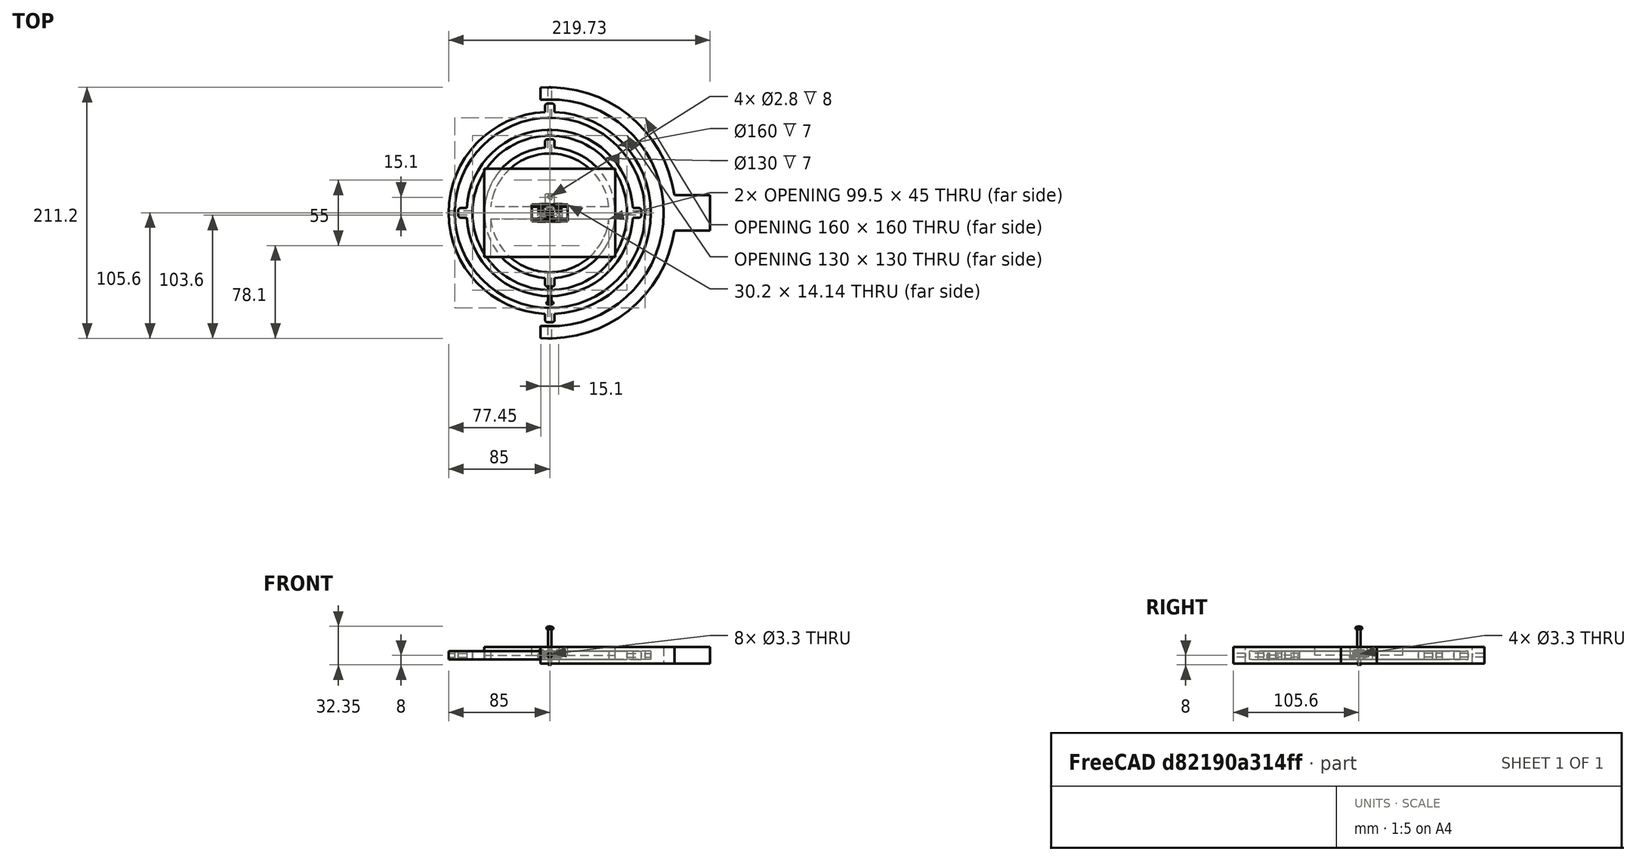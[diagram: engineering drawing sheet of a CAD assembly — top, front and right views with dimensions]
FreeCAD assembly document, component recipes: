
FREECAD ASSEMBLY — COMPONENT RECIPES ("calibration_jig_v1")

This assembly document has 17 components, labeled P0..P16 below (a component is one placed body or linked part). 10 of them carry a construction recipe — the FreeCAD feature program that regenerates the part from scratch, quoted from this document or its linked companion documents; the rest are supplied as boundary geometry only. No exploded tour is included for this assembly.
COMPONENT P0 — geometry summary ("GY_511_LSM303DLHC001"; no construction recipe available for this part):
  bounding box: 21.0 x 16.0 x 3.8 mm
  tessellated surface: 12,790 triangles
  volume: 549 mm^3 (43% of its bounding box)
COMPONENT P1 — geometry summary ("M3-Nut001"; no construction recipe available for this part):
  bounding box: 6.4 x 5.5 x 2.4 mm
  tessellated surface: 2,004 triangles
  volume: 51 mm^3 (60% of its bounding box)
  symmetry: 2-fold rotationally symmetric about the x axis; 2-fold rotationally symmetric about the y axis; 2-fold rotationally symmetric about the z axis; mirror-symmetric across its x mid-plane, y mid-plane, z mid-plane
COMPONENT P2 — geometry summary ("M3-Nut002"; no construction recipe available for this part):
  bounding box: 6.4 x 5.5 x 2.4 mm
  tessellated surface: 2,004 triangles
  volume: 51 mm^3 (60% of its bounding box)
  symmetry: 2-fold rotationally symmetric about the x axis; 2-fold rotationally symmetric about the y axis; 2-fold rotationally symmetric about the z axis; mirror-symmetric across its x mid-plane, y mid-plane, z mid-plane
COMPONENT P3 — geometry summary ("M3-Nut003"; no construction recipe available for this part):
  bounding box: 6.4 x 5.5 x 2.4 mm
  tessellated surface: 2,004 triangles
  volume: 51 mm^3 (60% of its bounding box)
  symmetry: 2-fold rotationally symmetric about the x axis; 2-fold rotationally symmetric about the y axis; 2-fold rotationally symmetric about the z axis; mirror-symmetric across its x mid-plane, y mid-plane, z mid-plane
COMPONENT P4 — geometry summary ("M3x20-Screw003"; no construction recipe available for this part):
  bounding box: 27.3 x 5.6 x 5.6 mm
  tessellated surface: 3,442 triangles
  volume: 221 mm^3 (26% of its bounding box)
  symmetry: 4-fold rotationally symmetric about the x axis; mirror-symmetric across its y mid-plane
COMPONENT P5 — geometry summary ("M3x20-Screw002"; no construction recipe available for this part):
  bounding box: 27.3 x 5.6 x 5.6 mm
  tessellated surface: 3,442 triangles
  volume: 221 mm^3 (26% of its bounding box)
  symmetry: 2-fold rotationally symmetric about the z axis; mirror-symmetric across its y mid-plane
COMPONENT P6 — geometry summary ("M3x25-Screw001"; no construction recipe available for this part):
  bounding box: 32.3 x 5.6 x 5.6 mm
  tessellated surface: 3,622 triangles
  volume: 256 mm^3 (25% of its bounding box)
  symmetry: 4-fold rotationally symmetric about the x axis; mirror-symmetric across its y mid-plane, z mid-plane
COMPONENT P7 — recipe-attached ("base001", modeled in this document).
Construction recipe (the document's own serialized feature program — sketch geometry with constraints, then the solid features built on it; lengths are millimeters unless a unit is written):

FEATURE [Sketcher::SketchObject] Sketch078
  ArcFitTolerance = 1e-06
  AttachmentSupport = -> [XY_Plane049]
  ExternalTypes = [0]
  FullyConstrained = true
  MakeInternals = false
  MapMode = 5
  expr: Constraints[20] = 2.02 * VarSet.Base_ring_depth
  expr: Constraints[21] = 3.02 * VarSet.Base_ring_width
  sketch-geometry (10):
    g0: LineSegment StartX=-15.1 StartY=7.07 StartZ=0 EndX=-15.1 EndY=-7.07 EndZ=0
    g1: LineSegment StartX=-15.1 StartY=-7.07 StartZ=0 EndX=15.1 EndY=-7.07 EndZ=0
    g2: LineSegment StartX=15.1 StartY=-7.07 StartZ=0 EndX=15.1 EndY=7.07 EndZ=0
    g3: LineSegment StartX=15.1 StartY=7.07 StartZ=0 EndX=-15.1 EndY=7.07 EndZ=0
    g4: GeomPoint [constr] X=0 Y=0 Z=0
    g5: LineSegment StartX=-55.1 StartY=37.07 StartZ=0 EndX=-55.1 EndY=-37.07 EndZ=0
    g6: LineSegment StartX=-55.1 StartY=-37.07 StartZ=0 EndX=55.1 EndY=-37.07 EndZ=0
    g7: LineSegment StartX=55.1 StartY=-37.07 StartZ=0 EndX=55.1 EndY=37.07 EndZ=0
    g8: LineSegment StartX=55.1 StartY=37.07 StartZ=0 EndX=-55.1 EndY=37.07 EndZ=0
    g9: GeomPoint [constr] X=0 Y=0 Z=0
  constraints (24):
    c: Coincident(g0,g1)
    c: Coincident(g1,g2)
    c: Coincident(g2,g3)
    c: Coincident(g3,g0)
    c: Vertical(g0)
    c: Vertical(g2)
    c: Horizontal(g1)
    c: Horizontal(g3)
    c: Symmetric(g2,g0,g4)
    c: Coincident(g4,g-1)
    c: Coincident(g5,g6)
    c: Coincident(g6,g7)
    c: Coincident(g7,g8)
    c: Coincident(g8,g5)
    c: Vertical(g5)
    c: Vertical(g7)
    c: Horizontal(g6)
    c: Horizontal(g8)
    c: Symmetric(g7,g5,g9)
    c: Coincident(g9,g4)
    c: DistanceY(g1,g2) = 14.14
    c: DistanceX(g0,g2) = 30.2
    c: DistanceX(g5,g0) = 40
    c: DistanceY(g0,g5) = 30
FEATURE [PartDesign::Pad] Pad009
  Direction = (0,0,1)
  Length = 7
  Length2 = 10
  Profile = -> Sketch078
  ReferenceAxis = -> Sketch078 [N_Axis]
  Refine = true
  Suppressed = false
  Type = 0
  expr: Length = VarSet.Base_ring_depth
FEATURE [PartDesign::Body] Body024  label="base"
  AllowCompound = false
  Group = -> [Sketch078,Pad009]
  Origin = -> Origin092
  Tip = -> Pad009
COMPONENT P8 — recipe-attached ("base_outside001", modeled in this document).
Construction recipe (the document's own serialized feature program — sketch geometry with constraints, then the solid features built on it; lengths are millimeters unless a unit is written):

FEATURE [Sketcher::SketchObject] Sketch077
  ArcFitTolerance = 1e-06
  AttachmentSupport = -> [XY_Plane048]
  ExternalTypes = [0]
  FullyConstrained = true
  MakeInternals = false
  MapMode = 5
  expr: Constraints[11] = 3 * VarSet.Base_ring_width
  expr: Constraints[20] = VarSet.Base_ring_base_diameter
  expr: Constraints[7] = VarSet.Base_ring_width
  sketch-geometry (15):
    g0: ArcOfCircle CenterX=0.199246 CenterY=2.76e-14 CenterZ=0 NormalX=0 NormalY=0 NormalZ=1 AngleXU=0 Radius=105.6 StartAngle=0.142528 EndAngle=1.64852
    g1: ArcOfCircle CenterX=0.199246 CenterY=2.05388e-11 CenterZ=0 NormalX=0 NormalY=0 NormalZ=1 AngleXU=0 Radius=105.6 StartAngle=4.63467 EndAngle=6.14066
    g2: LineSegment StartX=-8 StartY=105.281 StartZ=0 EndX=-8 EndY=95.2812 EndZ=0
    g3: LineSegment StartX=-8 StartY=-105.281 StartZ=0 EndX=-8 EndY=-95.2812 EndZ=0
    g4: LineSegment [constr] StartX=-8 StartY=-105.281 StartZ=0 EndX=-8 EndY=105.281 EndZ=0
    g5: LineSegment StartX=104.728 StartY=-15 StartZ=0 EndX=134.728 EndY=-15 EndZ=0
    g6: LineSegment StartX=134.728 StartY=-15 StartZ=0 EndX=134.728 EndY=15 EndZ=0
    g7: LineSegment StartX=134.728 StartY=15 StartZ=0 EndX=104.728 EndY=15 EndZ=0
    g8: LineSegment [constr] StartX=134.728 StartY=-15 StartZ=0 EndX=104.728 EndY=-15 EndZ=0
    g9: LineSegment [constr] StartX=134.728 StartY=15 StartZ=0 EndX=104.728 EndY=15 EndZ=0
    g10: ArcOfCircle CenterX=0.199246 CenterY=2.76e-14 CenterZ=0 NormalX=0 NormalY=0 NormalZ=1 AngleXU=0 Radius=95.6 StartAngle=4.79408 EndAngle=7.77229
    g11: LineSegment StartX=-8 StartY=-95.2812 StartZ=0 EndX=8 EndY=-95.2812 EndZ=0
    g12: LineSegment StartX=-8 StartY=95.2812 StartZ=0 EndX=8 EndY=95.2812 EndZ=0
    g13: LineSegment [constr] StartX=8 StartY=95.2812 StartZ=0 EndX=8 EndY=-95.2812 EndZ=0
    g14: LineSegment [constr] StartX=104.728 StartY=-15 StartZ=0 EndX=104.728 EndY=15 EndZ=0
  constraints (40):
    c: Coincident(g2,g0)
    c: Coincident(g3,g1)
    c: Coincident(g4,g1)
    c: Coincident(g4,g0)
    c: Vertical(g4)
    c: PointOnObject(g2,g4)
    c: Distance(g4,g-2) = 8
    c: DistanceY(g2,g0) = 10
    c: Equal(g3,g2)
    c: Coincident(g5,g6)
    c: Coincident(g6,g7)
    c: DistanceY(g5,g6) = 30
    c: Distance(g8,g5) = 30
    c: Horizontal(g5)
    c: Coincident(g1,g5)
    c: Horizontal(g7)
    c: Coincident(g0,g7)
    c: Coincident(g8,g5)
    c: Coincident(g9,g6)
    c: Coincident(g10,g0)
    c: Radius(g10) = 95.6
    c: Coincident(g11,g3)
    c: Coincident(g11,g10)
    c: Horizontal(g11)
    c: Coincident(g12,g2)
    c: Coincident(g12,g10)
    c: Horizontal(g12)
    c: Coincident(g13,g10)
    c: Coincident(g13,g10)
    c: Vertical(g13)
    c: Distance(g13,g4) = 16
    c: Symmetric(g5,g6,g-1)
    c: Coincident(g8,g1)
    c: Coincident(g14,g1)
    c: Coincident(g14,g0)
    c: Vertical(g14)
    c: Coincident(g9,g0)
    c: Symmetric(g2,g3,g-1)
    c: Distance(g0,g10) = 10
    c: Equal(g1,g0)
FEATURE [PartDesign::Pad] Pad008
  Direction = (0,0,1)
  Length = 14
  Length2 = 10
  Midplane = true
  Profile = -> Sketch077
  ReferenceAxis = -> Sketch077 [N_Axis]
  Refine = true
  Suppressed = false
  Type = 0
  expr: Length = 2 * VarSet.Base_ring_depth
FEATURE [Sketcher::SketchObject] Sketch079
  ArcFitTolerance = 1e-06
  AttachmentSupport = -> [XZ_Plane048]
  ExternalTypes = [0]
  FullyConstrained = true
  MakeInternals = false
  MapMode = 5
  Placement = pos=(0,0,0) rot=(1,0,0;1.5708rad)
  expr: Constraints[1] = VarSet.Base_ring_connector_scew
  sketch-geometry (1):
    g0: Circle CenterX=0 CenterY=0 CenterZ=0 NormalX=0 NormalY=0 NormalZ=1 AngleXU=0 Radius=1.65
  constraints (2):
    c: Coincident(g0,g-1)
    c: Diameter(g0) = 3.3
FEATURE [PartDesign::Pocket] Pocket006
  BaseFeature = -> Pad008
  Direction = (0,1,-2e-16)
  Length = 5
  Length2 = 5
  Midplane = true
  Profile = -> Sketch079
  ReferenceAxis = -> Sketch079 [N_Axis]
  Refine = true
  Suppressed = false
  Type = 1
FEATURE [PartDesign::Body] Body023  label="base_outside"
  AllowCompound = false
  Group = -> [Sketch077,Pad008,Sketch079,Pocket006]
  Origin = -> Origin090
  Tip = -> Pocket006
COMPONENT P9 — recipe-attached ("first_circle001", modeled in this document).
Construction recipe (the document's own serialized feature program — sketch geometry with constraints, then the solid features built on it; lengths are millimeters unless a unit is written):

FEATURE [Sketcher::SketchObject] Sketch
  ArcFitTolerance = 1e-06
  AttachmentSupport = -> [XY_Plane011]
  ExternalTypes = [0]
  FullyConstrained = true
  MakeInternals = false
  MapMode = 5
  expr: Constraints[2] = VarSet.Base_sensor_base_diameter
  expr: Constraints[3] = VarSet.Base_sensor_base_diameter + VarSet.Base_ring_width
  sketch-geometry (2):
    g0: Circle CenterX=0 CenterY=0 CenterZ=0 NormalX=0 NormalY=0 NormalZ=1 AngleXU=0 Radius=55
    g1: Circle CenterX=0 CenterY=0 CenterZ=0 NormalX=0 NormalY=0 NormalZ=1 AngleXU=0 Radius=50
  constraints (5):
    c: Coincident(g0,g-1)
    c: PointOnObject(g1,g-2)
    c: Diameter(g1) = 100
    c: Diameter(g0) = 110
    c: PointOnObject(g1,g-1)
FEATURE [PartDesign::Pad] Pad002
  Direction = (0,0,1)
  Length = 7
  Length2 = 10
  Midplane = true
  Profile = -> Sketch
  ReferenceAxis = -> Sketch [N_Axis]
  Refine = true
  Suppressed = false
  Type = 0
  expr: Length = VarSet.Base_ring_depth
FEATURE [Sketcher::SketchObject] Sketch069
  ArcFitTolerance = 1e-06
  AttachmentSupport = -> [XY_Plane011]
  ExternalTypes = [0]
  FullyConstrained = true
  MakeInternals = false
  MapMode = 5
  expr: Constraints[10] = VarSet.Base_sensor_base_diameter / 2
  expr: Constraints[7] = VarSet.Base_ring_connector_lenght
  expr: Constraints[8] = VarSet.Base_ring_connector_width
  sketch-geometry (4):
    g0: LineSegment StartX=-4 StartY=62 StartZ=0 EndX=-4 EndY=50 EndZ=0
    g1: LineSegment StartX=-4 StartY=50 StartZ=0 EndX=4 EndY=50 EndZ=0
    g2: LineSegment StartX=4 StartY=50 StartZ=0 EndX=4 EndY=62 EndZ=0
    g3: LineSegment StartX=4 StartY=62 StartZ=0 EndX=-4 EndY=62 EndZ=0
  constraints (11):
    c: Coincident(g0,g1)
    c: Coincident(g1,g2)
    c: Coincident(g2,g3)
    c: Coincident(g3,g0)
    c: Vertical(g0)
    c: Vertical(g2)
    c: Horizontal(g1)
    c: Distance(g0,g2) = 8
    c: Distance(g1,g3) = 12
    c: Symmetric(g0,g2,g-2)
    c: DistanceY(g-1,g1) = 50
FEATURE [PartDesign::Pad] Pad003
  BaseFeature = -> Pad002
  Direction = (0,0,1)
  Length = 7
  Length2 = 10
  Midplane = true
  Profile = -> Sketch069
  ReferenceAxis = -> Sketch069 [N_Axis]
  Refine = true
  Suppressed = false
  Type = 0
  expr: Length = VarSet.Base_ring_depth
FEATURE [PartDesign::Mirrored] Mirrored
  BaseFeature = -> Pad003
  MirrorPlane = -> Sketch069 [H_Axis]
  Originals = -> [Pad003]
  Refine = true
  Suppressed = false
  TransformMode = 0
FEATURE [Sketcher::SketchObject] Sketch081  label="sensor_base"
  ArcFitTolerance = 1e-06
  AttachmentSupport = -> [XY_Plane011]
  ExternalTypes = [0]
  FullyConstrained = true
  MakeInternals = false
  MapMode = 5
  expr: Constraints[20] = VarSet.Base_sensor_base_diameter * 1.1
  sketch-geometry (18):
    g0: Circle CenterX=7.55 CenterY=2.4 CenterZ=0 NormalX=0 NormalY=0 NormalZ=1 AngleXU=0 Radius=1.4
    g1: Circle CenterX=-7.55 CenterY=2.4 CenterZ=0 NormalX=0 NormalY=0 NormalZ=1 AngleXU=0 Radius=1.4
    g2: Circle CenterX=-7.55 CenterY=2.4 CenterZ=0 NormalX=0 NormalY=0 NormalZ=1 AngleXU=0 Radius=2.2
    g3: Circle CenterX=7.55 CenterY=2.4 CenterZ=0 NormalX=0 NormalY=0 NormalZ=1 AngleXU=0 Radius=2.2
    g4: GeomPoint X=-1e-16 Y=2.4 Z=0
    g5: LineSegment [constr] StartX=-1e-16 StartY=2.4 StartZ=0 EndX=-1e-16 EndY=-1.6 EndZ=0
    g6: LineSegment StartX=-55 StartY=-5 StartZ=0 EndX=55 EndY=-5 EndZ=0
    g7: LineSegment StartX=55 StartY=5 StartZ=0 EndX=-55 EndY=5 EndZ=0
    g8: Circle CenterX=0 CenterY=-2 CenterZ=0 NormalX=0 NormalY=0 NormalZ=1 AngleXU=0 Radius=2.2
    g9: LineSegment StartX=-55 StartY=5 StartZ=0 EndX=-55 EndY=-5 EndZ=0
    g10: LineSegment StartX=55 StartY=-5 StartZ=0 EndX=55 EndY=5 EndZ=0
    g11: Circle CenterX=0 CenterY=-2 CenterZ=0 NormalX=0 NormalY=0 NormalZ=1 AngleXU=0 Radius=1.4
    g12: Circle CenterX=0 CenterY=13.1 CenterZ=0 NormalX=0 NormalY=0 NormalZ=1 AngleXU=0 Radius=1.4
    g13: Circle CenterX=0 CenterY=13.1 CenterZ=0 NormalX=0 NormalY=0 NormalZ=1 AngleXU=0 Radius=2.2
    g14: LineSegment StartX=-4 StartY=16 StartZ=0 EndX=-4 EndY=4 EndZ=0
    g15: LineSegment StartX=-4 StartY=4 StartZ=0 EndX=4 EndY=4 EndZ=0
    g16: LineSegment StartX=4 StartY=4 StartZ=0 EndX=4 EndY=16 EndZ=0
    g17: LineSegment StartX=4 StartY=16 StartZ=0 EndX=-4 EndY=16 EndZ=0
  constraints (44):
    c: Diameter(g1) = 2.8
    c: Coincident(g2,g1)
    c: Coincident(g3,g0)
    c: Equal(g1,g0)
    c: Diameter(g2) = 4.4
    c: Equal(g2,g3)
    c: DistanceX(g1,g0) = 15.1
    c: Symmetric(g1,g0,g4)
    c: Coincident(g5,g4)
    c: Vertical(g5)
    c: DistanceY(g5,g1) = 4
    c: Horizontal(g7)
    c: Symmetric(g6,g6,g-2)
    c: DistanceY(g6,g7) = 10
    c: Symmetric(g6,g7,g-1)
    c: PointOnObject(g8,g-2)
    c: Equal(g3,g8)
    c: Distance(g-1,g8) = 2
    c: Symmetric(g1,g0,g-2)
    c: Distance(g3,g7) = 0.4
    c: DistanceX(g6,g6) = 110
    c: Coincident(g9,g7)
    c: Coincident(g9,g6)
    c: Coincident(g10,g6)
    c: Coincident(g10,g7)
    c: Vertical(g10)
    c: Coincident(g11,g8)
    c: PointOnObject(g12,g-2)
    c: Coincident(g13,g12)
    c: Equal(g8,g13)
    c: Equal(g1,g11)
    c: Equal(g11,g12)
    c: Distance(g8,g12) = 15.1
    c: Coincident(g14,g15)
    c: Coincident(g15,g16)
    c: Coincident(g16,g17)
    c: Coincident(g17,g14)
    c: Vertical(g14)
    c: Vertical(g16)
    c: Horizontal(g15)
    c: Symmetric(g14,g16,g-2)
    c: DistanceX(g14,g16) = 8
    c: Distance(g15,g7) = 1
    c: DistanceY(g15,g16) = 12
FEATURE [Sketcher::SketchObject] Sketch082
  ArcFitTolerance = 1e-06
  AttachmentSupport = -> [XZ_Plane011]
  ExternalTypes = [0]
  FullyConstrained = true
  MakeInternals = false
  MapMode = 5
  Placement = pos=(0,0,0) rot=(1,0,0;1.5708rad)
  expr: Constraints[1] = VarSet.Base_ring_connector_scew
  sketch-geometry (1):
    g0: Circle CenterX=0 CenterY=0 CenterZ=0 NormalX=0 NormalY=0 NormalZ=1 AngleXU=0 Radius=1.65
  constraints (2):
    c: Coincident(g0,g-1)
    c: Diameter(g0) = 3.3
FEATURE [PartDesign::Pocket] Pocket007
  BaseFeature = -> Mirrored
  Direction = (0,1,-2e-16)
  Length = 5
  Length2 = 5
  Midplane = true
  Profile = -> Sketch082
  ReferenceAxis = -> Sketch082 [N_Axis]
  Refine = true
  Suppressed = false
  Type = 1
FEATURE [PartDesign::Pad] Pad011
  BaseFeature = -> Pocket007
  Direction = (0,0,1)
  Length = 7
  Length2 = 10
  Midplane = true
  Profile = -> Sketch081 [Edge7,Edge6,Edge5,Edge8]
  ReferenceAxis = -> Sketch081 [N_Axis]
  Refine = true
  Suppressed = false
  Type = 0
  expr: Length = VarSet.Base_ring_depth
FEATURE [PartDesign::Pad] Pad012
  BaseFeature = -> Pad011
  Direction = (0,0,1)
  Length = 7
  Length2 = 10
  Midplane = true
  Profile = -> Sketch081 [Edge14,Edge13,Edge15,Edge16]
  ReferenceAxis = -> Sketch081 [N_Axis]
  Refine = true
  Suppressed = false
  Type = 0
  expr: Length = VarSet.Base_ring_depth
FEATURE [PartDesign::Pad] Pad013
  BaseFeature = -> Pad012
  Direction = (0,0,1)
  Length = 4.5
  Length2 = 10
  Profile = -> Sketch081 [Edge12,Edge3,Edge4,Edge9]
  ReferenceAxis = -> Sketch081 [N_Axis]
  Refine = true
  Suppressed = false
  Type = 0
  expr: Length = VarSet.Base_ring_depth / 2 + 1 mm
FEATURE [PartDesign::Pocket] Pocket008
  BaseFeature = -> Pad013
  Direction = (0,0,-1)
  Length = 5
  Length2 = 5
  Midplane = true
  Profile = -> Sketch081 [Edge1,Edge11,Edge2,Edge10]
  ReferenceAxis = -> Sketch081 [N_Axis]
  Refine = true
  Suppressed = false
  Type = 1
FEATURE [PartDesign::Fillet] Fillet
  Base = -> Pocket008 [Edge69,Edge70,Edge83,Edge84]
  BaseFeature = -> Pocket008
  Radius = 2
  Refine = true
  SupportTransform = false
  Suppressed = false
  UseAllEdges = false
FEATURE [PartDesign::Body] Body  label="first_circle"
  AllowCompound = false
  Group = -> [Sketch,Pad002,Sketch069,Pad003,Mirrored,Sketch081,Sketch082,Pocket007,Pad011,Pad012,Pad013,Pocket008,Fillet]
  Origin = -> Origin022
  Tip = -> Fillet
COMPONENT P10 — recipe-attached ("second_cicle001", modeled in this document).
Construction recipe (the document's own serialized feature program — sketch geometry with constraints, then the solid features built on it; lengths are millimeters unless a unit is written):

FEATURE [Sketcher::SketchObject] Sketch071
  ArcFitTolerance = 1e-06
  AttachmentSupport = -> [XY_Plane046]
  ExternalTypes = [0]
  FullyConstrained = true
  MakeInternals = false
  MapMode = 5
  expr: Constraints[13] = VarSet.Base_ring_connector_width
  expr: Constraints[14] = VarSet.Base_ring_connector_lenght
  expr: Constraints[2] = VarSet.Base_second_ring_diameter
  expr: Constraints[3] = VarSet.Base_second_ring_diameter + VarSet.Base_ring_width
  sketch-geometry (10):
    g0: Circle CenterX=0 CenterY=0 CenterZ=0 NormalX=0 NormalY=0 NormalZ=1 AngleXU=0 Radius=70
    g1: Circle CenterX=0 CenterY=0 CenterZ=0 NormalX=0 NormalY=0 NormalZ=1 AngleXU=0 Radius=65
    g2: LineSegment StartX=65 StartY=4 StartZ=0 EndX=65 EndY=-4 EndZ=0
    g3: LineSegment StartX=65 StartY=-4 StartZ=0 EndX=77 EndY=-4 EndZ=0
    g4: LineSegment StartX=77 StartY=-4 StartZ=0 EndX=77 EndY=4 EndZ=0
    g5: LineSegment StartX=77 StartY=4 StartZ=0 EndX=65 EndY=4 EndZ=0
    g6: LineSegment StartX=-77 StartY=4 StartZ=0 EndX=-65 EndY=4 EndZ=0
    g7: LineSegment StartX=-65 StartY=4 StartZ=0 EndX=-65 EndY=-4 EndZ=0
    g8: LineSegment StartX=-65 StartY=-4 StartZ=0 EndX=-77 EndY=-4 EndZ=0
    g9: LineSegment StartX=-77 StartY=-4 StartZ=0 EndX=-77 EndY=4 EndZ=0
  constraints (26):
    c: Coincident(g0,g-1)
    c: Coincident(g1,g0)
    c: Diameter(g1) = 130
    c: Diameter(g0) = 140
    c: Coincident(g2,g3)
    c: Coincident(g3,g4)
    c: Coincident(g4,g5)
    c: Coincident(g5,g2)
    c: Vertical(g4)
    c: Horizontal(g3)
    c: Horizontal(g5)
    c: Symmetric(g2,g2,g-1)
    c: Tangent(g2,g1)
    c: DistanceX(g2,g3) = 12
    c: DistanceY(g3,g4) = 8
    c: Coincident(g7,g8)
    c: Coincident(g8,g9)
    c: Coincident(g9,g6)
    c: Coincident(g6,g7)
    c: Vertical(g9)
    c: Horizontal(g8)
    c: Horizontal(g6)
    c: Equal(g3,g8)
    c: Equal(g9,g4)
    c: Symmetric(g7,g6,g-1)
    c: Tangent(g7,g1)
FEATURE [PartDesign::Pad] Pad004
  Direction = (0,0,1)
  Length = 7
  Length2 = 10
  Midplane = true
  Profile = -> Sketch071 [Edge1,Edge2]
  ReferenceAxis = -> Sketch071 [N_Axis]
  Refine = true
  Suppressed = false
  Type = 0
  expr: Length = VarSet.Base_ring_depth
FEATURE [PartDesign::Pad] Pad005
  BaseFeature = -> Pad004
  Direction = (0,0,1)
  Length = 7
  Length2 = 10
  Midplane = true
  Profile = -> Sketch071 [Edge7,Edge8,Edge9,Edge10,Edge3,Edge6,Edge5,Edge4]
  ReferenceAxis = -> Sketch071 [N_Axis]
  Refine = true
  Suppressed = false
  Type = 0
  expr: Length = VarSet.Base_ring_depth
FEATURE [Sketcher::SketchObject] Sketch073
  ArcFitTolerance = 1e-06
  AttachmentSupport = -> [XZ_Plane046]
  ExternalTypes = [0]
  FullyConstrained = true
  MakeInternals = false
  MapMode = 5
  Placement = pos=(0,0,0) rot=(1,0,0;1.5708rad)
  expr: Constraints[1] = VarSet.Base_ring_connector_scew
  sketch-geometry (1):
    g0: Circle CenterX=0 CenterY=0 CenterZ=0 NormalX=0 NormalY=0 NormalZ=1 AngleXU=0 Radius=1.65
  constraints (2):
    c: Coincident(g0,g-1)
    c: Diameter(g0) = 3.3
FEATURE [PartDesign::Pocket] Pocket003
  BaseFeature = -> Pad005
  Direction = (0,1,-2e-16)
  Length = 5
  Length2 = 5
  Midplane = true
  Profile = -> Sketch073
  ReferenceAxis = -> Sketch073 [N_Axis]
  Refine = true
  Suppressed = false
  Type = 1
FEATURE [Sketcher::SketchObject] Sketch084
  ArcFitTolerance = 1e-06
  AttachmentSupport = -> [YZ_Plane046]
  ExternalTypes = [0]
  FullyConstrained = true
  MakeInternals = false
  MapMode = 5
  Placement = pos=(0,0,0) rot=(0.57735,0.57735,0.57735;2.0944rad)
  expr: Constraints[1] = VarSet.Base_ring_connector_scew
  sketch-geometry (1):
    g0: Circle CenterX=0 CenterY=0 CenterZ=0 NormalX=0 NormalY=0 NormalZ=1 AngleXU=0 Radius=1.65
  constraints (2):
    c: Coincident(g0,g-1)
    c: Diameter(g0) = 3.3
FEATURE [PartDesign::Pocket] Pocket010
  BaseFeature = -> Pocket003
  Direction = (-1,0,0)
  Length = 5
  Length2 = 5
  Midplane = true
  Profile = -> Sketch084
  ReferenceAxis = -> Sketch084 [N_Axis]
  Refine = true
  Suppressed = false
  Type = 1
FEATURE [PartDesign::Fillet] Fillet002
  Base = -> Pocket010 [Edge25,Edge4,Edge30,Edge31]
  BaseFeature = -> Pocket010
  Radius = 2
  Refine = true
  SupportTransform = false
  Suppressed = false
  UseAllEdges = false
FEATURE [PartDesign::Body] Body021  label="second_cicle"
  AllowCompound = false
  Group = -> [Sketch071,Pad004,Pad005,Sketch073,Pocket003,Sketch084,Pocket010,Fillet002]
  Origin = -> Origin086
  Tip = -> Fillet002
COMPONENT P11 — recipe-attached ("space001", modeled in this document).
Construction recipe (the document's own serialized feature program — sketch geometry with constraints, then the solid features built on it; lengths are millimeters unless a unit is written):

FEATURE [Sketcher::SketchObject] Sketch080
  ArcFitTolerance = 1e-06
  AttachmentSupport = -> [XY_Plane050]
  ExternalTypes = [0]
  FullyConstrained = true
  MakeInternals = false
  MapMode = 5
  expr: Constraints[2] = VarSet.Base_ring_connector_scew
  sketch-geometry (2):
    g0: Circle CenterX=0 CenterY=0 CenterZ=0 NormalX=0 NormalY=0 NormalZ=1 AngleXU=0 Radius=1.65
    g1: Circle CenterX=0 CenterY=0 CenterZ=0 NormalX=0 NormalY=0 NormalZ=1 AngleXU=0 Radius=3.65
  constraints (4):
    c: Coincident(g0,g-1)
    c: Coincident(g1,g0)
    c: Diameter(g0) = 3.3
    c: Distance(g0,g1) = 2
FEATURE [PartDesign::Pad] Pad010
  Direction = (0,0,1)
  Length = 2
  Length2 = 10
  Midplane = true
  Profile = -> Sketch080
  ReferenceAxis = -> Sketch080 [N_Axis]
  Refine = true
  Suppressed = false
  Type = 0
FEATURE [PartDesign::Body] Body025  label="space"
  AllowCompound = false
  Group = -> [Sketch080,Pad010]
  Origin = -> Origin094
  Tip = -> Pad010
COMPONENT P12 — same part as P11; its construction recipe is shown at P11.
COMPONENT P13 — same part as P11; its construction recipe is shown at P11.
COMPONENT P14 — same part as P11; its construction recipe is shown at P11.
COMPONENT P15 — same part as P11; its construction recipe is shown at P11.
COMPONENT P16 — recipe-attached ("third_circle001", modeled in this document).
Construction recipe (the document's own serialized feature program — sketch geometry with constraints, then the solid features built on it; lengths are millimeters unless a unit is written):

FEATURE [Sketcher::SketchObject] Sketch074
  ArcFitTolerance = 1e-06
  AttachmentSupport = -> [XY_Plane047]
  ExternalTypes = [0]
  FullyConstrained = true
  MakeInternals = false
  MapMode = 5
  expr: Constraints[12] = VarSet.Base_ring_connector_lenght
  expr: Constraints[13] = VarSet.Base_ring_connector_width
  expr: Constraints[1] = VarSet.Base_third_ring_diameter
  expr: Constraints[23] = VarSet.Base_ring_connector_width
  expr: Constraints[24] = VarSet.Base_ring_connector_lenght
  expr: Constraints[2] = VarSet.Base_third_ring_diameter + VarSet.Base_ring_width
  sketch-geometry (10):
    g0: Circle CenterX=0 CenterY=0 CenterZ=0 NormalX=0 NormalY=0 NormalZ=1 AngleXU=0 Radius=85
    g1: Circle CenterX=0 CenterY=0 CenterZ=0 NormalX=0 NormalY=0 NormalZ=1 AngleXU=0 Radius=80
    g2: LineSegment StartX=-4 StartY=92 StartZ=0 EndX=-4 EndY=80 EndZ=0
    g3: LineSegment StartX=-4 StartY=80 StartZ=0 EndX=4 EndY=80 EndZ=0
    g4: LineSegment StartX=4 StartY=80 StartZ=0 EndX=4 EndY=92 EndZ=0
    g5: LineSegment StartX=4 StartY=92 StartZ=0 EndX=-4 EndY=92 EndZ=0
    g6: LineSegment StartX=-4 StartY=-80 StartZ=0 EndX=-4 EndY=-92 EndZ=0
    g7: LineSegment StartX=-4 StartY=-92 StartZ=0 EndX=4 EndY=-92 EndZ=0
    g8: LineSegment StartX=4 StartY=-92 StartZ=0 EndX=4 EndY=-80 EndZ=0
    g9: LineSegment StartX=4 StartY=-80 StartZ=0 EndX=-4 EndY=-80 EndZ=0
  constraints (26):
    c: Coincident(g1,g0)
    c: Diameter(g1) = 160
    c: Diameter(g0) = 170
    c: Coincident(g0,g-1)
    c: Coincident(g2,g3)
    c: Coincident(g3,g4)
    c: Coincident(g4,g5)
    c: Coincident(g5,g2)
    c: Vertical(g2)
    c: Vertical(g4)
    c: Horizontal(g5)
    c: Symmetric(g2,g3,g-2)
    c: DistanceX(g2,g3) = 8
    c: DistanceY(g3,g4) = 12
    c: Tangent(g3,g1)
    c: Coincident(g6,g7)
    c: Coincident(g7,g8)
    c: Coincident(g8,g9)
    c: Coincident(g9,g6)
    c: Vertical(g6)
    c: Vertical(g8)
    c: Horizontal(g9)
    c: Symmetric(g7,g6,g-2)
    c: DistanceY(g6,g6) = 12
    c: DistanceX(g6,g8) = 8
    c: Tangent(g9,g1)
FEATURE [Sketcher::SketchObject] Sketch075
  ArcFitTolerance = 1e-06
  AttachmentSupport = -> [XZ_Plane047]
  ExternalTypes = [0]
  FullyConstrained = true
  MakeInternals = false
  MapMode = 5
  Placement = pos=(0,0,0) rot=(1,0,0;1.5708rad)
  expr: Constraints[1] = VarSet.Base_ring_connector_scew
  sketch-geometry (1):
    g0: Circle CenterX=0 CenterY=0 CenterZ=0 NormalX=0 NormalY=0 NormalZ=1 AngleXU=0 Radius=1.65
  constraints (2):
    c: Coincident(g0,g-1)
    c: Diameter(g0) = 3.3
FEATURE [Sketcher::SketchObject] Sketch076
  ArcFitTolerance = 1e-06
  AttachmentSupport = -> [YZ_Plane047]
  ExternalTypes = [0]
  FullyConstrained = true
  MakeInternals = false
  MapMode = 5
  Placement = pos=(0,0,0) rot=(0.57735,0.57735,0.57735;2.0944rad)
  expr: Constraints[1] = VarSet.Base_ring_connector_scew
  sketch-geometry (1):
    g0: Circle CenterX=0 CenterY=0 CenterZ=0 NormalX=0 NormalY=0 NormalZ=1 AngleXU=0 Radius=1.65
  constraints (2):
    c: Coincident(g0,g-1)
    c: Diameter(g0) = 3.3
FEATURE [PartDesign::Pad] Pad006
  Direction = (0,0,1)
  Length = 7
  Length2 = 10
  Midplane = true
  Profile = -> Sketch074 [Edge2,Edge1]
  ReferenceAxis = -> Sketch074 [N_Axis]
  Refine = true
  Suppressed = false
  Type = 0
  expr: Length = VarSet.Base_ring_depth
FEATURE [PartDesign::Pad] Pad007
  BaseFeature = -> Pad006
  Direction = (0,0,1)
  Length = 7
  Length2 = 10
  Midplane = true
  Profile = -> Sketch074 [Edge4,Edge3,Edge5,Edge6,Edge10,Edge7,Edge8,Edge9]
  ReferenceAxis = -> Sketch074 [N_Axis]
  Refine = true
  Suppressed = false
  Type = 0
  expr: Length = VarSet.Base_ring_depth
FEATURE [PartDesign::Pocket] Pocket004
  BaseFeature = -> Pad007
  Direction = (-1,0,0)
  Length = 5
  Length2 = 5
  Midplane = true
  Profile = -> Sketch076
  ReferenceAxis = -> Sketch076 [N_Axis]
  Refine = true
  Suppressed = false
  Type = 1
FEATURE [PartDesign::Pocket] Pocket005
  BaseFeature = -> Pocket004
  Direction = (0,1,-2e-16)
  Length = 5
  Length2 = 5
  Midplane = true
  Profile = -> Sketch075
  ReferenceAxis = -> Sketch075 [N_Axis]
  Refine = true
  Suppressed = false
  Type = 1
FEATURE [PartDesign::Fillet] Fillet001
  Base = -> Pocket005 [Edge4,Edge31,Edge36,Edge37]
  BaseFeature = -> Pocket005
  Radius = 2
  Refine = true
  SupportTransform = false
  Suppressed = false
  UseAllEdges = false
FEATURE [PartDesign::Body] Body022  label="third_circle"
  AllowCompound = false
  Group = -> [Sketch074,Sketch075,Sketch076,Pad006,Pad007,Pocket004,Pocket005,Fillet001]
  Origin = -> Origin088
  Tip = -> Fillet001
PROVENANCE & LICENSES
A FreeCAD (.FCStd) document from a public repository crawl; recipes are the document's own serialized feature recipes (and, for linked parts, companion documents' recipes).
License: mit.
